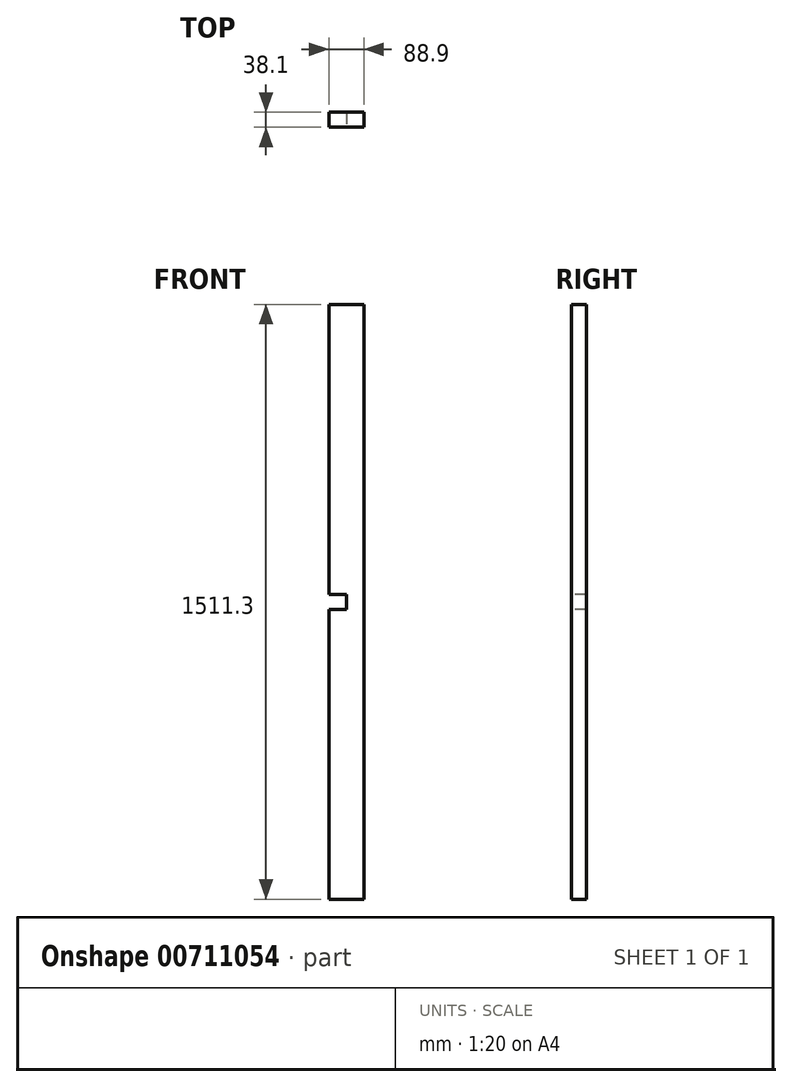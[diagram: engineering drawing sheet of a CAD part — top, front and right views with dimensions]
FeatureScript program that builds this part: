
annotation { "Feature Type Name" : "Feature", "Feature Type Description" : "" }
export const myFeature = defineFeature(function(context is Context, id is Id, definition is map)
    precondition{}
    {
        {
            var Q0;
            Q0=qCreatedBy(makeId("Top.planeOp"),FACE);
            var sketch = newSketch(context, id + "F0", { "sketchPlane" : qUnion([Q0])});
            skLineSegment(sketch, "E0.bottom", {"start": v(47.99, 19.05) * mm, "end": v(-40.91, 19.05) * mm});
            skLineSegment(sketch, "E0.top", {"start": v(47.99, -19.05) * mm, "end": v(-40.91, -19.05) * mm});
            skLineSegment(sketch, "E0.left", {"start": v(47.99, 19.05) * mm, "end": v(47.99, -19.05) * mm});
            skLineSegment(sketch, "E0.right", {"start": v(-40.91, 19.05) * mm, "end": v(-40.91, -19.05) * mm});
            skPoint(sketch, "E0.middle", {"position": v(3.54, 0) * mm});
            skSolve(sketch);
        }
        {
            var Q0;
            Q0 = qSketchRegion(id + "F0", true);
            extrude(context, id + "F1", {"entities" : qUnion([Q0]), "depth" : 1511.3 * mm, "offsetDistance" : 25.4 * mm});
        }
        {
            var Q0;
            Q0=makeQuery(id+"F1.opExtrude","SWEPT_FACE",FACE,{"disambiguationData":[OSD([sQuery(id+"F0.wireOp",EDGE,"E0.right")])]});
            var sketch = newSketch(context, id + "F2", { "sketchPlane" : qUnion([Q0])});
            skLineSegment(sketch, "E1.0", {"start": v(-19.05, 774.7) * mm, "end": v(19.05, 774.7) * mm});
            skLineSegment(sketch, "E2.0", {"start": v(-19.05, 736.6) * mm, "end": v(19.05, 736.6) * mm});
            skPoint(sketch, "E3.end.orphan", {"position": v(19.05, 755.65) * mm});
            skPoint(sketch, "E3.start.orphan", {"position": v(-19.05, 755.65) * mm});
            skSolve(sketch);
        }
        {
            var Q0;
            Q0 = qSketchRegion(id + "F2", true);
            var Q1;
            {var subQ0=sQuery(id+"F2.wireOp",EDGE,"E1.0");Q1=makeQuery(id+"F2.imprint","IMPRINT",FACE,{"disambiguationData":[TD([[makeQuery(id+"F2.imprint","IMPRINT",EDGE,{"derivedFrom":subQ0}),-1.0]])]});}
            extrude(context, id + "F3", {"entities" : qUnion([Q0, Q1]), "operationType" : NewBodyOperationType.REMOVE, "oppositeDirection" : true, "depth" : 44.45 * mm, "offsetDistance" : 25.4 * mm});
        }
    });
